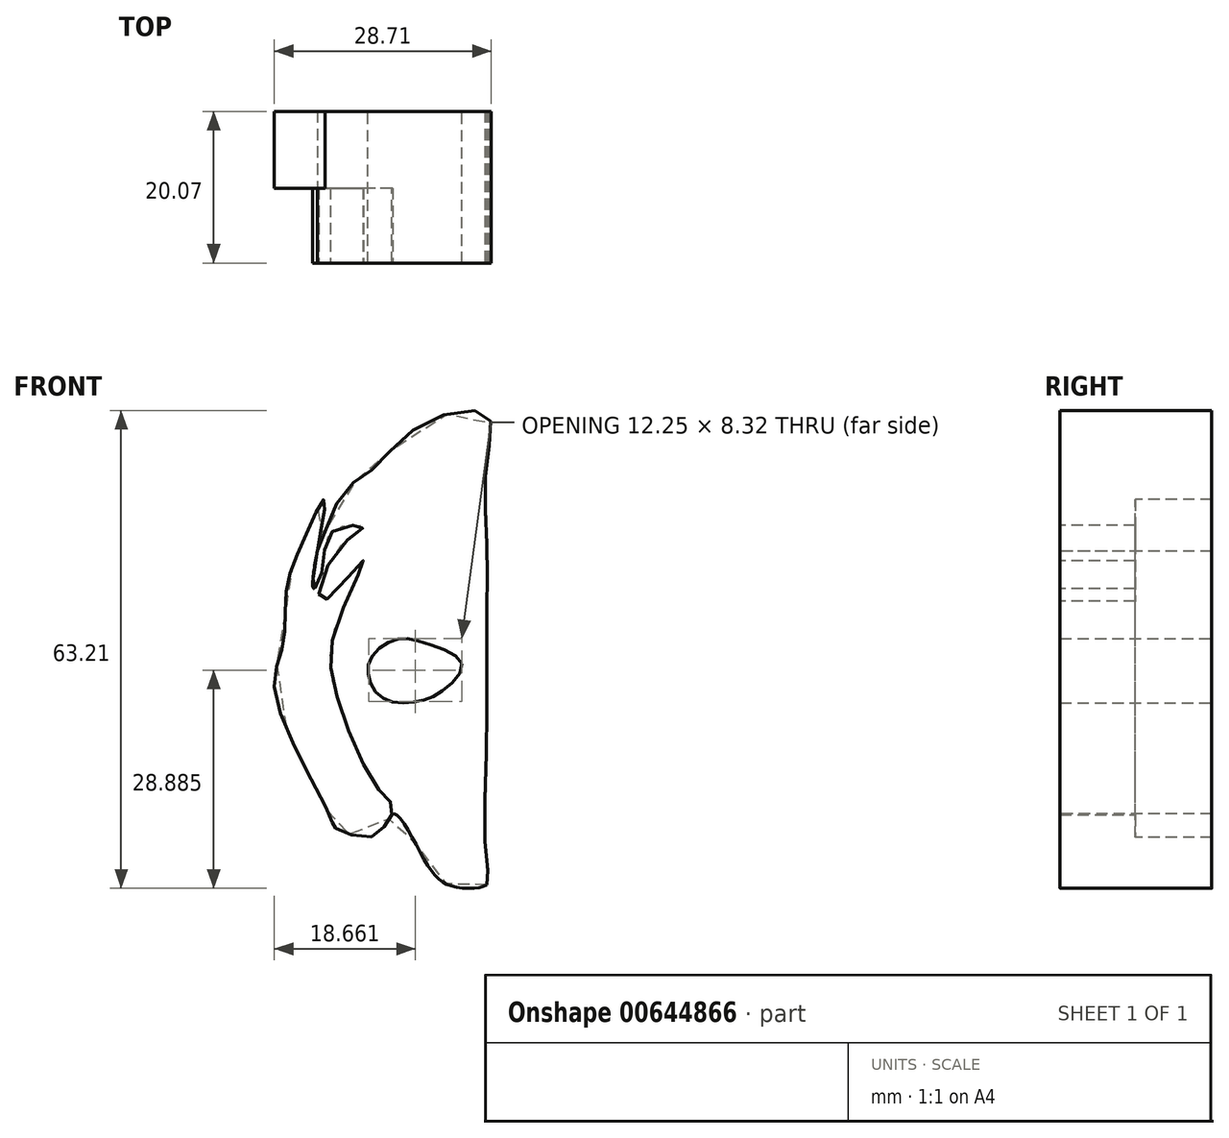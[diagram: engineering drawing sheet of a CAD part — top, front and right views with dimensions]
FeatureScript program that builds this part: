
annotation { "Feature Type Name" : "Feature", "Feature Type Description" : "" }
export const myFeature = defineFeature(function(context is Context, id is Id, definition is map)
    precondition{}
    {
        {
            var Q0;
            Q0=qCreatedBy(makeId("Front.planeOp"),FACE);
            var sketch = newSketch(context, id + "F0", { "sketchPlane" : qUnion([Q0])});
            skPoint(sketch, "E0.16.internal.snap0", {"position": v(0, 76.38) * mm});
            skPoint(sketch, "E0.17.internal.snap0", {"position": v(0, 76.38) * mm});
            skPoint(sketch, "E0.18.internal.snap0", {"position": v(0, 76.38) * mm});
            skPoint(sketch, "E0.19.internal.snap0", {"position": v(0, 76.38) * mm});
            skPoint(sketch, "E0.20.internal.snap0", {"position": v(0, 76.38) * mm});
            skPoint(sketch, "E0.21.internal.snap0", {"position": v(0, 76.38) * mm});
            skFitSpline(sketch, "E0", {"points": [v(0, 12.12) * mm, v(-4.41, 11.88) * mm, v(-8, 15) * mm, v(-12.33, 21.47) * mm, v(-14.72, 18.6) * mm, v(-20.24, 19.79) * mm, v(-20.48, 20.5) * mm, v(-27.91, 36.81) * mm, v(-26.95, 44) * mm, v(-26.47, 51.2) * mm, v(-23.84, 58.63) * mm, v(-21.44, 62.95) * mm, v(-22.4, 56.24) * mm, v(-19.52, 63.2) * mm, v(-15.2, 67.03) * mm, v(-8.49, 73.02) * mm, v(0, 74.22) * mm, v(0, 68.23) * mm, v(0, 56.72) * mm, v(0, 46.17) * mm, v(0, 32.74) * mm, v(0, 15) * mm, v(0, 12.12) * mm]});
            skFitSpline(sketch, "E1", {"points": [v(-3.33, 41.37) * mm, v(-5.99, 37.65) * mm, v(-9.44, 36.32) * mm, v(-13.42, 36.59) * mm, v(-15.55, 39.24) * mm, v(-15.28, 42.16) * mm, v(-12.1, 44.55) * mm, v(-8, 44.02) * mm, v(-3.33, 41.37) * mm]});
            skSolve(sketch);
        }
        {
            var Q0;
            Q0=makeQuery(id+"F0.imprint","IMPRINT",FACE,{"disambiguationData":[TD([[makeQuery(id+"F0.imprint","IMPRINT",EDGE,{"derivedFrom":sQuery(id+"F0.wireOp",EDGE,"E0")}),-1.0]])]});
            var sketch = newSketch(context, id + "F1", { "sketchPlane" : qUnion([Q0])});
            skFitSpline(sketch, "E2", {"points": [v(-12.46, 22.48) * mm, v(-14.15, 24.46) * mm, v(-19.8, 36.88) * mm, v(-19.8, 46.76) * mm, v(-16.4, 54.95) * mm, v(-21.77, 49.58) * mm, v(-19.8, 56.36) * mm, v(-16.4, 59.46) * mm, v(-20.36, 58.9) * mm, v(-21.77, 53.82) * mm, v(-22.9, 51.28) * mm, v(-22.05, 57.77) * mm, v(-20.92, 62.85) * mm, v(-24.03, 58.9) * mm, v(-26.57, 51.28) * mm, v(-27.42, 43.37) * mm, v(-28.26, 37.16) * mm, v(-25.44, 33.78) * mm, v(-18.95, 19.1) * mm, v(-14.15, 19.1) * mm, v(-12.46, 22.48) * mm]});
            skSolve(sketch);
        }
        {
            var Q0;
            Q0=makeQuery(id+"F1.imprint","IMPRINT",FACE,{"disambiguationData":[TD([[makeQuery(id+"F1.imprint","IMPRINT",EDGE,{"derivedFrom":makeQuery(id+"F0.imprint","IMPRINT",EDGE,{"derivedFrom":sQuery(id+"F0.wireOp",EDGE,"E1")})}),1.0]])]});
            extrude(context, id + "F2", {"entities" : qUnion([Q0]), "depth" : 20.07 * mm, "offsetDistance" : 25.4 * mm});
        }
        {
            var Q0;
            Q0=makeQuery(id+"F0.imprint","IMPRINT",FACE,{"disambiguationData":[TD([[makeQuery(id+"F0.imprint","IMPRINT",EDGE,{"derivedFrom":sQuery(id+"F0.wireOp",EDGE,"E0")}),-1.0]])]});
            extrude(context, id + "F3", {"entities" : qUnion([Q0]), "operationType" : NewBodyOperationType.ADD, "depth" : 10.16 * mm, "offsetDistance" : 25.4 * mm});
        }
    });
